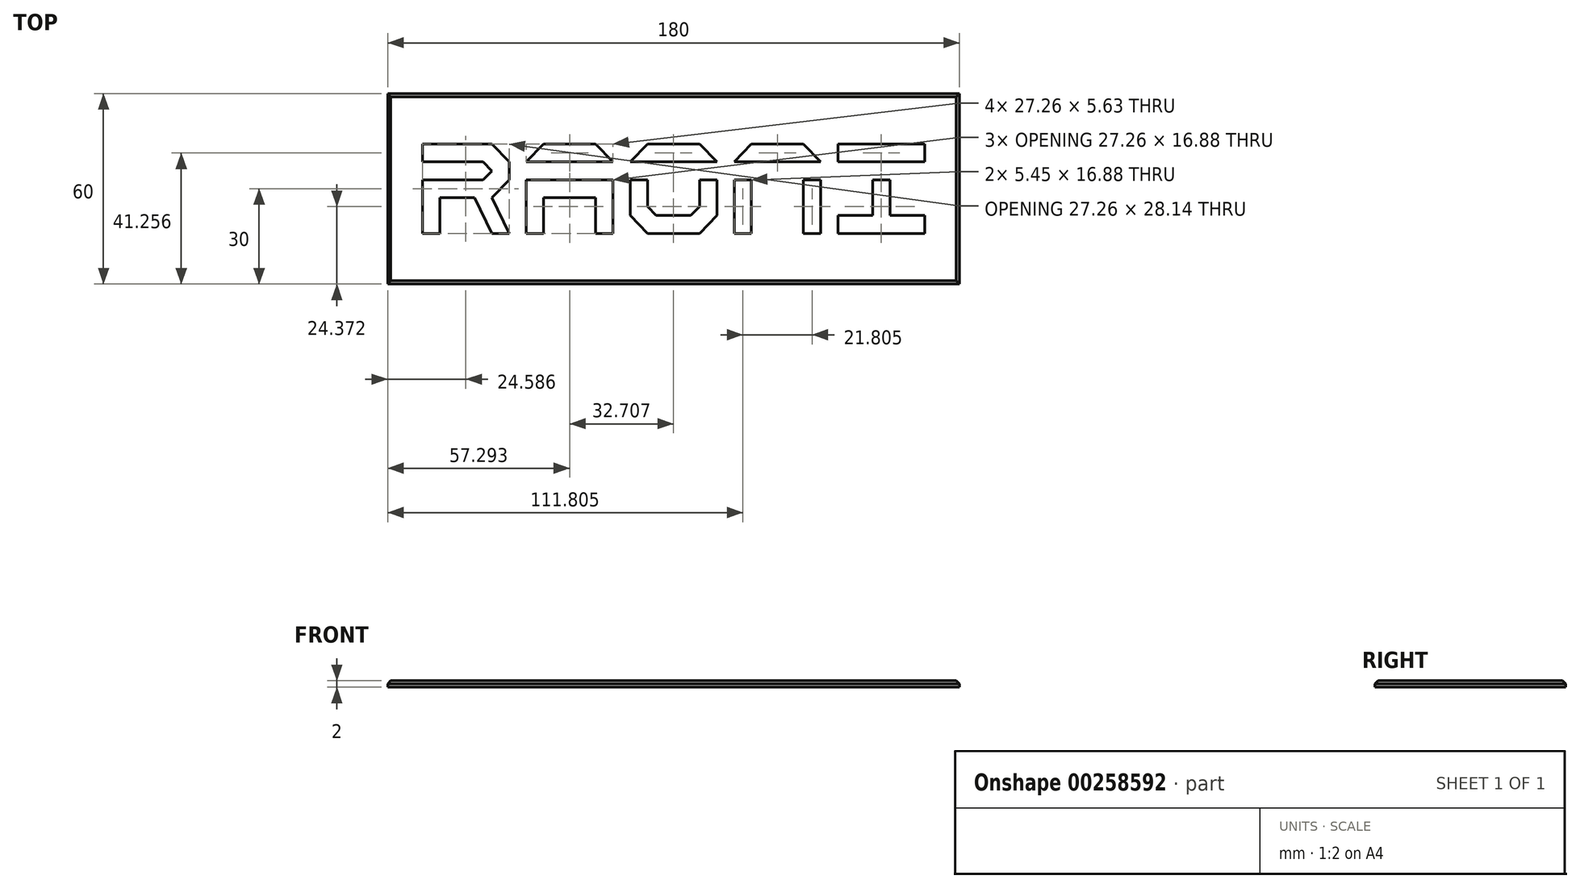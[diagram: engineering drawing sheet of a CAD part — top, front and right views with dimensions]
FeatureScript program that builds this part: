
annotation { "Feature Type Name" : "Feature", "Feature Type Description" : "" }
export const myFeature = defineFeature(function(context is Context, id is Id, definition is map)
    precondition{}
    {
        {
            var Q0;
            Q0=qCreatedBy(makeId("Front.planeOp"),FACE);
            var sketch = newSketch(context, id + "F0", { "sketchPlane" : qUnion([Q0])});
            skLineSegment(sketch, "E0", {"start": v(25, -25) * mm, "end": v(-25, -25) * mm});
            skLineSegment(sketch, "E1", {"start": v(-25, -25) * mm, "end": v(-25, 25) * mm});
            skLineSegment(sketch, "E2", {"start": v(-25, 25) * mm, "end": v(25, 25) * mm});
            skLineSegment(sketch, "E3", {"start": v(25, 25) * mm, "end": v(25, -25) * mm});
            skLineSegment(sketch, "E4", {"start": v(-1.53, -13.36) * mm, "end": v(-1.53, -12.36) * mm});
            skLineSegment(sketch, "E5", {"start": v(-1.53, -12.36) * mm, "end": v(-5.5, -12.36) * mm});
            skLineSegment(sketch, "E6", {"start": v(-5.5, -12.36) * mm, "end": v(-5.5, -16.36) * mm});
            skLineSegment(sketch, "E7", {"start": v(-5.5, -16.36) * mm, "end": v(-4.5, -16.36) * mm});
            skLineSegment(sketch, "E8", {"start": v(-4.5, -16.36) * mm, "end": v(-4.5, -13.36) * mm});
            skLineSegment(sketch, "E9", {"start": v(-4.5, -13.36) * mm, "end": v(-1.53, -13.36) * mm});
            skLineSegment(sketch, "E10", {"start": v(-14.02, -12.36) * mm, "end": v(-14.02, -16.36) * mm});
            skLineSegment(sketch, "E11", {"start": v(-14.02, -16.36) * mm, "end": v(-13.01, -16.36) * mm});
            skLineSegment(sketch, "E12", {"start": v(-13.01, -16.36) * mm, "end": v(-13.01, -13.36) * mm});
            skLineSegment(sketch, "E13", {"start": v(-13.01, -13.36) * mm, "end": v(-10.58, -13.36) * mm});
            skLineSegment(sketch, "E14", {"start": v(-10.58, -13.36) * mm, "end": v(-10.58, -13.36) * mm});
            skLineSegment(sketch, "E15", {"start": v(-10.58, -13.36) * mm, "end": v(-10.55, -13.36) * mm});
            skLineSegment(sketch, "E16", {"start": v(-10.55, -13.36) * mm, "end": v(-10.55, -16.36) * mm});
            skLineSegment(sketch, "E17", {"start": v(-10.55, -16.36) * mm, "end": v(-9.55, -16.36) * mm});
            skLineSegment(sketch, "E18", {"start": v(-9.55, -16.36) * mm, "end": v(-9.55, -13.36) * mm});
            skLineSegment(sketch, "E19", {"start": v(-9.55, -13.36) * mm, "end": v(-9.51, -13.36) * mm});
            skLineSegment(sketch, "E20", {"start": v(-9.51, -13.36) * mm, "end": v(-9.51, -13.36) * mm});
            skLineSegment(sketch, "E21", {"start": v(-9.51, -13.36) * mm, "end": v(-7.08, -13.36) * mm});
            skLineSegment(sketch, "E22", {"start": v(-7.08, -13.36) * mm, "end": v(-7.08, -16.36) * mm});
            skLineSegment(sketch, "E23", {"start": v(-7.08, -16.36) * mm, "end": v(-6.08, -16.36) * mm});
            skLineSegment(sketch, "E24", {"start": v(-6.08, -16.36) * mm, "end": v(-6.08, -12.36) * mm});
            skLineSegment(sketch, "E25", {"start": v(-6.08, -12.36) * mm, "end": v(-14.02, -12.36) * mm});
            skLineSegment(sketch, "E26", {"start": v(10.27, -12.36) * mm, "end": v(10.27, -13.36) * mm});
            skLineSegment(sketch, "E27", {"start": v(10.27, -13.36) * mm, "end": v(11.5, -13.36) * mm});
            skLineSegment(sketch, "E28", {"start": v(11.5, -13.36) * mm, "end": v(11.5, -12.36) * mm});
            skLineSegment(sketch, "E29", {"start": v(11.5, -12.36) * mm, "end": v(10.27, -12.36) * mm});
            skLineSegment(sketch, "E30", {"start": v(7.56, -12.36) * mm, "end": v(6.56, -12.36) * mm});
            skLineSegment(sketch, "E31", {"start": v(6.56, -12.36) * mm, "end": v(3.56, -12.36) * mm});
            skLineSegment(sketch, "E32", {"start": v(3.56, -12.36) * mm, "end": v(3.56, -13.36) * mm});
            skLineSegment(sketch, "E33", {"start": v(3.56, -13.36) * mm, "end": v(6.56, -13.36) * mm});
            skLineSegment(sketch, "E34", {"start": v(6.56, -13.36) * mm, "end": v(6.56, -16.36) * mm});
            skLineSegment(sketch, "E35", {"start": v(6.56, -16.36) * mm, "end": v(7.56, -16.36) * mm});
            skLineSegment(sketch, "E36", {"start": v(7.56, -16.36) * mm, "end": v(7.56, -13.36) * mm});
            skLineSegment(sketch, "E37", {"start": v(7.56, -13.36) * mm, "end": v(8.76, -13.36) * mm});
            skLineSegment(sketch, "E38", {"start": v(8.76, -13.36) * mm, "end": v(9.7, -13.36) * mm});
            skLineSegment(sketch, "E39", {"start": v(9.7, -13.36) * mm, "end": v(9.7, -12.36) * mm});
            skLineSegment(sketch, "E40", {"start": v(9.7, -12.36) * mm, "end": v(8.76, -12.36) * mm});
            skLineSegment(sketch, "E41", {"start": v(8.76, -12.36) * mm, "end": v(7.56, -12.36) * mm});
            skLineSegment(sketch, "E42", {"start": v(12.06, -12.36) * mm, "end": v(12.06, -16.36) * mm});
            skLineSegment(sketch, "E43", {"start": v(12.06, -16.36) * mm, "end": v(15.75, -16.36) * mm});
            skLineSegment(sketch, "E44", {"start": v(15.75, -16.36) * mm, "end": v(15.75, -15.35) * mm});
            skLineSegment(sketch, "E45", {"start": v(15.75, -15.35) * mm, "end": v(13.06, -15.35) * mm});
            skLineSegment(sketch, "E46", {"start": v(13.06, -15.35) * mm, "end": v(13.06, -13.36) * mm});
            skLineSegment(sketch, "E47", {"start": v(13.06, -13.36) * mm, "end": v(19, -13.36) * mm});
            skLineSegment(sketch, "E48", {"start": v(19, -13.36) * mm, "end": v(19, -15.35) * mm});
            skLineSegment(sketch, "E49", {"start": v(19, -15.35) * mm, "end": v(16.32, -15.35) * mm});
            skLineSegment(sketch, "E50", {"start": v(16.32, -15.35) * mm, "end": v(16.32, -16.36) * mm});
            skLineSegment(sketch, "E51", {"start": v(16.32, -16.36) * mm, "end": v(16.5, -16.36) * mm});
            skLineSegment(sketch, "E52", {"start": v(16.5, -16.36) * mm, "end": v(17.76, -16.36) * mm});
            skLineSegment(sketch, "E53", {"start": v(17.76, -16.36) * mm, "end": v(20, -16.36) * mm});
            skLineSegment(sketch, "E54", {"start": v(20, -16.36) * mm, "end": v(20, -12.36) * mm});
            skLineSegment(sketch, "E55", {"start": v(20, -12.36) * mm, "end": v(12.06, -12.36) * mm});
            skLineSegment(sketch, "E56", {"start": v(3, -12.36) * mm, "end": v(1.53, -12.36) * mm});
            skLineSegment(sketch, "E57", {"start": v(1.53, -12.36) * mm, "end": v(0.03, -13.86) * mm});
            skLineSegment(sketch, "E58", {"start": v(0.03, -13.86) * mm, "end": v(0.03, -12.36) * mm});
            skLineSegment(sketch, "E59", {"start": v(0.03, -12.36) * mm, "end": v(-0.04, -12.36) * mm});
            skLineSegment(sketch, "E60", {"start": v(-0.04, -12.36) * mm, "end": v(-0.98, -12.36) * mm});
            skLineSegment(sketch, "E61", {"start": v(-0.98, -12.36) * mm, "end": v(-0.98, -16.36) * mm});
            skLineSegment(sketch, "E62", {"start": v(-0.98, -16.36) * mm, "end": v(0.03, -16.36) * mm});
            skLineSegment(sketch, "E63", {"start": v(0.03, -16.36) * mm, "end": v(0.03, -14.85) * mm});
            skLineSegment(sketch, "E64", {"start": v(0.03, -14.85) * mm, "end": v(1.53, -16.36) * mm});
            skLineSegment(sketch, "E65", {"start": v(1.53, -16.36) * mm, "end": v(3, -16.36) * mm});
            skLineSegment(sketch, "E66", {"start": v(3, -16.36) * mm, "end": v(0.99, -14.36) * mm});
            skLineSegment(sketch, "E67", {"start": v(0.99, -14.36) * mm, "end": v(3, -12.36) * mm});
            skSolve(sketch);
        }
        {
            var Q0;
            Q0=qCreatedBy(makeId("Top.planeOp"),FACE);
            var sketch = newSketch(context, id + "F1", { "sketchPlane" : qUnion([Q0])});
            skLineSegment(sketch, "E68", {"start": v(68.14, 2.81) * mm, "end": v(62.69, 2.81) * mm});
            skLineSegment(sketch, "E69", {"start": v(62.69, 2.81) * mm, "end": v(62.69, -8.44) * mm});
            skLineSegment(sketch, "E70", {"start": v(62.69, -8.44) * mm, "end": v(51.79, -8.44) * mm});
            skLineSegment(sketch, "E71", {"start": v(51.79, -8.44) * mm, "end": v(51.79, -14.07) * mm});
            skLineSegment(sketch, "E72", {"start": v(51.79, -14.07) * mm, "end": v(79.04, -14.07) * mm});
            skLineSegment(sketch, "E73", {"start": v(79.04, -14.07) * mm, "end": v(79.04, -8.44) * mm});
            skLineSegment(sketch, "E74", {"start": v(79.04, -8.44) * mm, "end": v(68.14, -8.44) * mm});
            skLineSegment(sketch, "E75", {"start": v(68.14, -8.44) * mm, "end": v(68.14, 2.81) * mm});
            skLineSegment(sketch, "E76", {"start": v(51.79, 14.07) * mm, "end": v(51.79, 8.44) * mm});
            skLineSegment(sketch, "E77", {"start": v(51.79, 8.44) * mm, "end": v(79.04, 8.44) * mm});
            skLineSegment(sketch, "E78", {"start": v(79.04, 8.44) * mm, "end": v(79.04, 14.07) * mm});
            skLineSegment(sketch, "E79", {"start": v(79.04, 14.07) * mm, "end": v(51.79, 14.07) * mm});
            skLineSegment(sketch, "E80", {"start": v(40.88, -14.07) * mm, "end": v(46.34, -14.07) * mm});
            skLineSegment(sketch, "E81", {"start": v(46.34, -14.07) * mm, "end": v(46.34, 2.81) * mm});
            skLineSegment(sketch, "E82", {"start": v(46.34, 2.81) * mm, "end": v(40.88, 2.81) * mm});
            skLineSegment(sketch, "E83", {"start": v(40.88, 2.81) * mm, "end": v(40.88, -14.07) * mm});
            skLineSegment(sketch, "E84", {"start": v(19.08, -14.07) * mm, "end": v(24.53, -14.07) * mm});
            skLineSegment(sketch, "E85", {"start": v(24.53, -14.07) * mm, "end": v(24.53, 2.81) * mm});
            skLineSegment(sketch, "E86", {"start": v(24.53, 2.81) * mm, "end": v(19.08, 2.81) * mm});
            skLineSegment(sketch, "E87", {"start": v(19.08, 2.81) * mm, "end": v(19.08, -14.07) * mm});
            skLineSegment(sketch, "E88", {"start": v(24.53, 14.07) * mm, "end": v(19.08, 8.44) * mm});
            skLineSegment(sketch, "E89", {"start": v(19.08, 8.44) * mm, "end": v(46.34, 8.44) * mm});
            skLineSegment(sketch, "E90", {"start": v(46.34, 8.44) * mm, "end": v(40.88, 14.07) * mm});
            skLineSegment(sketch, "E91", {"start": v(40.88, 14.07) * mm, "end": v(24.53, 14.07) * mm});
            skLineSegment(sketch, "E92", {"start": v(8.18, -5.63) * mm, "end": v(5.45, -8.44) * mm});
            skLineSegment(sketch, "E93", {"start": v(5.45, -8.44) * mm, "end": v(-5.45, -8.44) * mm});
            skLineSegment(sketch, "E94", {"start": v(-5.45, -8.44) * mm, "end": v(-8.18, -5.63) * mm});
            skLineSegment(sketch, "E95", {"start": v(-8.18, -5.63) * mm, "end": v(-8.18, 2.81) * mm});
            skLineSegment(sketch, "E96", {"start": v(-8.18, 2.81) * mm, "end": v(-13.63, 2.81) * mm});
            skLineSegment(sketch, "E97", {"start": v(-13.63, 2.81) * mm, "end": v(-13.63, -8.44) * mm});
            skLineSegment(sketch, "E98", {"start": v(-13.63, -8.44) * mm, "end": v(-8.18, -14.07) * mm});
            skLineSegment(sketch, "E99", {"start": v(-8.18, -14.07) * mm, "end": v(8.18, -14.07) * mm});
            skLineSegment(sketch, "E100", {"start": v(8.18, -14.07) * mm, "end": v(13.63, -8.44) * mm});
            skLineSegment(sketch, "E101", {"start": v(13.63, -8.44) * mm, "end": v(13.63, 2.81) * mm});
            skLineSegment(sketch, "E102", {"start": v(13.63, 2.81) * mm, "end": v(8.18, 2.81) * mm});
            skLineSegment(sketch, "E103", {"start": v(8.18, 2.81) * mm, "end": v(8.18, -5.63) * mm});
            skLineSegment(sketch, "E104", {"start": v(-8.18, 14.07) * mm, "end": v(-13.63, 8.44) * mm});
            skLineSegment(sketch, "E105", {"start": v(-13.63, 8.44) * mm, "end": v(13.63, 8.44) * mm});
            skLineSegment(sketch, "E106", {"start": v(13.63, 8.44) * mm, "end": v(8.18, 14.07) * mm});
            skLineSegment(sketch, "E107", {"start": v(8.18, 14.07) * mm, "end": v(-8.18, 14.07) * mm});
            skLineSegment(sketch, "E108", {"start": v(-46.34, -14.07) * mm, "end": v(-40.88, -14.07) * mm});
            skLineSegment(sketch, "E109", {"start": v(-40.88, -14.07) * mm, "end": v(-40.88, -2.81) * mm});
            skLineSegment(sketch, "E110", {"start": v(-40.88, -2.81) * mm, "end": v(-24.53, -2.81) * mm});
            skLineSegment(sketch, "E111", {"start": v(-24.53, -2.81) * mm, "end": v(-24.53, -14.07) * mm});
            skLineSegment(sketch, "E112", {"start": v(-24.53, -14.07) * mm, "end": v(-19.08, -14.07) * mm});
            skLineSegment(sketch, "E113", {"start": v(-19.08, -14.07) * mm, "end": v(-19.08, 2.81) * mm});
            skLineSegment(sketch, "E114", {"start": v(-19.08, 2.81) * mm, "end": v(-46.34, 2.81) * mm});
            skLineSegment(sketch, "E115", {"start": v(-46.34, 2.81) * mm, "end": v(-46.34, -14.07) * mm});
            skLineSegment(sketch, "E116", {"start": v(-40.88, 14.07) * mm, "end": v(-46.34, 8.44) * mm});
            skLineSegment(sketch, "E117", {"start": v(-46.34, 8.44) * mm, "end": v(-19.08, 8.44) * mm});
            skLineSegment(sketch, "E118", {"start": v(-19.08, 8.44) * mm, "end": v(-24.53, 14.07) * mm});
            skLineSegment(sketch, "E119", {"start": v(-24.53, 14.07) * mm, "end": v(-40.88, 14.07) * mm});
            skLineSegment(sketch, "E120", {"start": v(-79.04, 14.07) * mm, "end": v(-79.04, 8.44) * mm});
            skLineSegment(sketch, "E121", {"start": v(-79.04, 8.44) * mm, "end": v(-59.96, 8.44) * mm});
            skLineSegment(sketch, "E122", {"start": v(-59.96, 8.44) * mm, "end": v(-57.24, 5.63) * mm});
            skLineSegment(sketch, "E123", {"start": v(-57.24, 5.63) * mm, "end": v(-59.96, 2.81) * mm});
            skLineSegment(sketch, "E124", {"start": v(-59.96, 2.81) * mm, "end": v(-79.04, 2.81) * mm});
            skLineSegment(sketch, "E125", {"start": v(-79.04, 2.81) * mm, "end": v(-79.04, -14.07) * mm});
            skLineSegment(sketch, "E126", {"start": v(-79.04, -14.07) * mm, "end": v(-73.6, -14.07) * mm});
            skLineSegment(sketch, "E127", {"start": v(-73.6, -14.07) * mm, "end": v(-73.6, -2.81) * mm});
            skLineSegment(sketch, "E128", {"start": v(-73.6, -2.81) * mm, "end": v(-62.69, -2.81) * mm});
            skLineSegment(sketch, "E129", {"start": v(-62.69, -2.81) * mm, "end": v(-57.24, -14.07) * mm});
            skLineSegment(sketch, "E130", {"start": v(-57.24, -14.07) * mm, "end": v(-51.79, -14.07) * mm});
            skLineSegment(sketch, "E131", {"start": v(-51.79, -14.07) * mm, "end": v(-57.24, -2.81) * mm});
            skLineSegment(sketch, "E132", {"start": v(-57.24, -2.81) * mm, "end": v(-51.79, 2.81) * mm});
            skLineSegment(sketch, "E133", {"start": v(-51.79, 2.81) * mm, "end": v(-51.79, 8.44) * mm});
            skLineSegment(sketch, "E134", {"start": v(-51.79, 8.44) * mm, "end": v(-57.24, 14.07) * mm});
            skLineSegment(sketch, "E135", {"start": v(-57.24, 14.07) * mm, "end": v(-79.04, 14.07) * mm});
            skLineSegment(sketch, "E136.bottom", {"start": v(90, -30) * mm, "end": v(-90, -30) * mm});
            skLineSegment(sketch, "E136.top", {"start": v(90, 30) * mm, "end": v(-90, 30) * mm});
            skLineSegment(sketch, "E136.left", {"start": v(90, -30) * mm, "end": v(90, 30) * mm});
            skLineSegment(sketch, "E136.right", {"start": v(-90, -30) * mm, "end": v(-90, 30) * mm});
            skPoint(sketch, "E136.middle", {"position": v(0, 0) * mm});
            skSolve(sketch);
        }
        {
            var Q0;
            Q0=makeQuery(id+"F1.imprint","IMPRINT",FACE,{"disambiguationData":[TD([[makeQuery(id+"F1.imprint","IMPRINT",EDGE,{"derivedFrom":sQuery(id+"F1.wireOp",EDGE,"E68")}),-1.0]])]});
            extrude(context, id + "F2", {"entities" : qUnion([Q0]), "depth" : 2 * mm});
        }
        {
            var Q0;
            Q0=makeQuery(id+"F2.opExtrude","CAP_EDGE",EDGE,{"disambiguationData":[OSD([sQuery(id+"F1.wireOp",EDGE,"E136.top")])],"isStart":false});
            var Q1;
            Q1=makeQuery(id+"F2.opExtrude","CAP_EDGE",EDGE,{"disambiguationData":[OSD([sQuery(id+"F1.wireOp",EDGE,"E136.bottom")])],"isStart":false});
            var Q2;
            Q2=makeQuery(id+"F2.opExtrude","CAP_EDGE",EDGE,{"disambiguationData":[OSD([sQuery(id+"F1.wireOp",EDGE,"E136.left")])],"isStart":false});
            var Q3;
            Q3=makeQuery(id+"F2.opExtrude","CAP_EDGE",EDGE,{"disambiguationData":[OSD([sQuery(id+"F1.wireOp",EDGE,"E136.right")])],"isStart":false});
            chamfer(context, id + "F3", {"entities" : qUnion([Q0, Q1, Q2, Q3]), "width" : 1 * mm, "tangentPropagation" : true});
        }
    });
